# Revit family: XLHC
name_source: partatom
category: Sprinklers
revit_build: Autodesk Revit MEP 2016 (Build: 20150220_1215(x64)
units: mm (PartAtom-declared; Revit-internal decimal feet)

## family parameters
Always vertical = Yes
Cut with Voids When Loaded = No
Maintain Annotation Orientation = No
OmniClass Number = 23.85.30.21
OmniClass Title = Environmental Detection/Registration
Part Type = Normal
Room Calculation Point = No
Round Connector Dimension = Use Diameter
Shared = No
Work Plane-Based = No

## types (1)
- RASCO XL INST HSW
    Coverage = Standard
    Description = CHROME FINISH
    Diameter = 5"
    K-Factor = 5.6
    Manufacturer = RASCO
    Model = XL INST HSW
    Orifice = Standard
    Orifice Size = 0"
    Pressure Class = Standard
    Pressure Rating = 21.6
    RASCO Part # = XLHC
    RASCO SIN # = R1334
    Response = Quick
    Temperature Rating = 165 °F

## geometry (parser evidence)
native form markers: Sweep x26
no freeform markers — native parametric forms only
